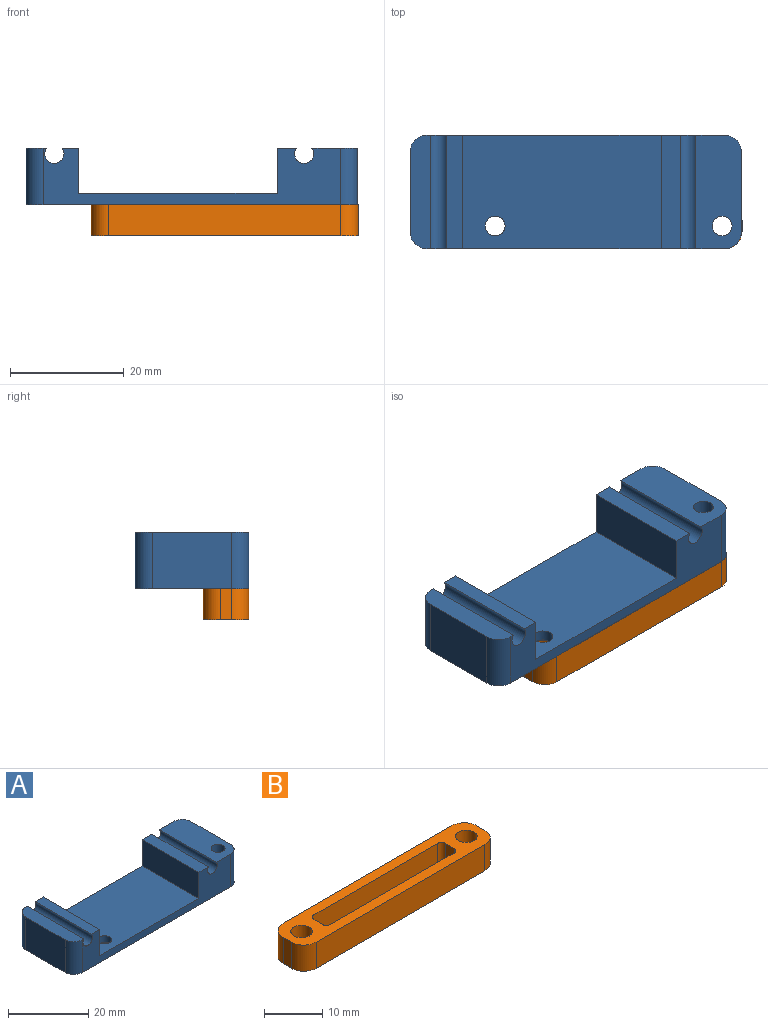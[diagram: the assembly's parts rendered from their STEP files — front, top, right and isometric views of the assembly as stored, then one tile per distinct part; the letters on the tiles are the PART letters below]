
ASSEMBLY  parts=2 mates=1
PART A: 20 faces, bbox 58.4x20x10 mm
  f0: plane 20x3.37mm, normal (0,0,1), area 67.5mm2, adj f1,f2,f7,f11
  f1: plane 52.41x10mm, normal (0,-1,0), area 228.6mm2, adj f0,f3,f4,f6,f7,f8,f10,f11
  f2: plane 52.41x10mm, normal (0,1,0), area 228.6mm2, adj f0,f3,f4,f6,f7,f8,f10,f11
  f3: plane 20x2.88mm, normal (0,0,1), area 57.5mm2, adj f1,f2,f8,f12
  f4: plane 20x8.03mm, normal (0,0,1), area 147.2mm2, adj f1,f2,f7,f9,f15,f16,f17
  f5: plane 14x10mm, normal (-1,0,0), area 140mm2, adj f6,f10,f18,f19
  f6: plane 20x3.63mm, normal (0,0,1), area 68.6mm2, adj f1,f2,f5,f8,f18,f19
  f7: cylinder r=1.7mm len=20mm, axis (0,-1,0), area 149.6mm2, adj f0,f1,f2,f4
  f8: cylinder r=1.7mm len=20mm, axis (0,-1,0), area 149.6mm2, adj f1,f2,f3,f6
  f9: plane 14x10mm, normal (1,0,0), area 140mm2, adj f4,f10,f16,f17
  f10: plane 58.41x20mm, normal (0,0,-1), area 1141.2mm2, adj f1,f2,f5,f9,f14,f15,f16,f17
  f11: plane 20x8mm, normal (-1,0,0), area 160mm2, adj f0,f1,f2,f13
  f12: plane 20x8mm, normal (1,0,0), area 160mm2, adj f1,f2,f3,f13
  f13: plane 35x20mm, normal (0,0,1), area 690.4mm2, adj f1,f2,f11,f12,f14
  f14: cylinder r=1.75mm len=3.5mm, axis (0,0,-1), area 22mm2, adj f10,f13
  f15: cylinder r=1.75mm len=10mm, axis (0,0,-1), area 110mm2, adj f4,f10
  f16: cylinder r=3mm len=10mm, axis (0,0,-1), area 47.1mm2, adj f2,f4,f9,f10
  f17: cylinder r=3mm len=10mm, axis (0,0,1), area 47.1mm2, adj f1,f4,f9,f10
  f18: cylinder r=3mm len=10mm, axis (0,0,-1), area 47.1mm2, adj f2,f5,f6,f10
  f19: cylinder r=3mm len=10mm, axis (0,0,1), area 47.1mm2, adj f1,f5,f6,f10
PART B: 20 faces, bbox 47x8x5.5 mm
  f0: plane 5.5x2mm, normal (-1,0,0), area 11mm2, adj f10,f11,f16,f19
  f1: plane 30x5.5mm, normal (0,1,0), area 165mm2, adj f10,f11,f16,f17
  f2: plane 5.5x2mm, normal (1,0,0), area 11mm2, adj f10,f11,f17,f18
  f3: plane 41x5.5mm, normal (0,-1,0), area 225.5mm2, adj f10,f11,f12,f15
  f4: plane 5.5x2mm, normal (1,0,0), area 11mm2, adj f10,f11,f12,f13
  f5: plane 41x5.5mm, normal (0,1,0), area 225.5mm2, adj f10,f11,f13,f14
  f6: plane 5.5x2mm, normal (-1,0,0), area 11mm2, adj f10,f11,f14,f15
  f7: cylinder r=1.85mm len=5.5mm, axis (0,0,-1), area 63.9mm2, adj f10,f11
  f8: cylinder r=1.85mm len=5.5mm, axis (0,0,-1), area 63.9mm2, adj f10,f11
  f9: plane 30x5.5mm, normal (0,-1,0), area 165mm2, adj f10,f11,f18,f19
  f10: plane 47x8mm, normal (0,0,1), area 219.6mm2, adj f0,f1,f2,f3,f4,f5,f6,f7
  f11: plane 47x8mm, normal (0,0,-1), area 219.6mm2, adj f0,f1,f2,f3,f4,f5,f6,f7
  f12: cylinder r=3mm len=5.5mm, axis (0,0,-1), area 25.9mm2, adj f3,f4,f10,f11
  f13: cylinder r=3mm len=5.5mm, axis (0,0,1), area 25.9mm2, adj f4,f5,f10,f11
  f14: cylinder r=3mm len=5.5mm, axis (0,0,-1), area 25.9mm2, adj f5,f6,f10,f11
  f15: cylinder r=3mm len=5.5mm, axis (0,0,1), area 25.9mm2, adj f3,f6,f10,f11
  f16: cylinder r=1mm len=5.5mm, axis (0,0,1), area 8.6mm2, adj f0,f1,f10,f11
  f17: cylinder r=1mm len=5.5mm, axis (0,0,-1), area 8.6mm2, adj f1,f2,f10,f11
  f18: cylinder r=1mm len=5.5mm, axis (0,0,1), area 8.6mm2, adj f2,f9,f10,f11
  f19: cylinder r=1mm len=5.5mm, axis (0,0,-1), area 8.6mm2, adj f0,f9,f10,f11
PLACE A t=(-14.51,-5.78,2.95)mm
PLACE B t=(-29.51,-11.78,7.45)mm
MATE slider A.f15 <-> B.f8  axis (0,0,-1) through (-9.51,-11.78,12.95)mm
